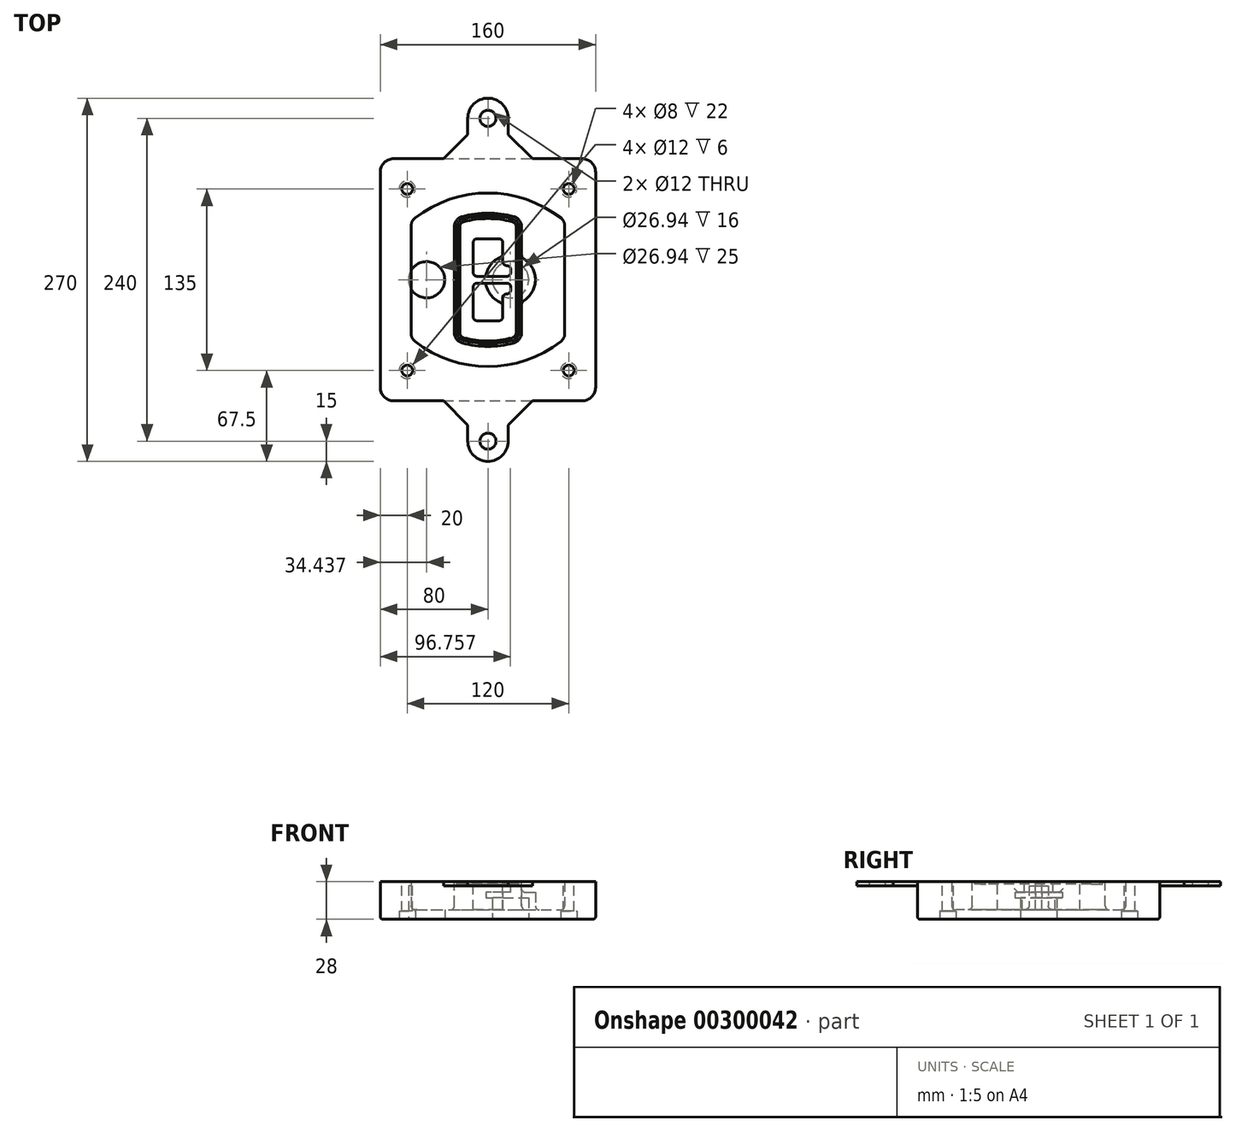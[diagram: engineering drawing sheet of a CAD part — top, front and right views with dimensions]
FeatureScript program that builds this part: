
annotation { "Feature Type Name" : "Feature", "Feature Type Description" : "" }
export const myFeature = defineFeature(function(context is Context, id is Id, definition is map)
    precondition{}
    {
        {
            var Q0;
            Q0=qCreatedBy(makeId("Top.planeOp"),FACE);
            var sketch = newSketch(context, id + "F0", { "sketchPlane" : qUnion([Q0])});
            skPoint(sketch, "E0.rect.middle", {"position": v(0, 0) * mm});
            skLineSegment(sketch, "E1.bottom", {"start": v(-70, -90) * mm, "end": v(70, -90) * mm});
            skLineSegment(sketch, "E1.top", {"start": v(-70, 90) * mm, "end": v(70, 90) * mm});
            skLineSegment(sketch, "E1.left", {"start": v(-80, -80) * mm, "end": v(-80, 80) * mm});
            skLineSegment(sketch, "E1.right", {"start": v(80, -80) * mm, "end": v(80, 80) * mm});
            skLineSegment(sketch, "E2", {"start": v(-80, 90) * mm, "end": v(80, -90) * mm, "construction": true});
            skLineSegment(sketch, "E3", {"start": v(80, 90) * mm, "end": v(-80, -90) * mm, "construction": true});
            skCircle(sketch, "E4", {"center": v(-60, 67.5) * mm, "radius": 4 * mm});
            skCircle(sketch, "E5", {"center": v(60, 67.5) * mm, "radius": 4 * mm});
            skCircle(sketch, "E6", {"center": v(60, -67.5) * mm, "radius": 4 * mm});
            skCircle(sketch, "E7", {"center": v(-60, -67.5) * mm, "radius": 4 * mm});
            skLineSegment(sketch, "E8", {"start": v(-60, 67.5) * mm, "end": v(60, 67.5) * mm, "construction": true});
            skLineSegment(sketch, "E9", {"start": v(60, 67.5) * mm, "end": v(60, -67.5) * mm, "construction": true});
            skLineSegment(sketch, "E10", {"start": v(60, -67.5) * mm, "end": v(-60, -67.5) * mm, "construction": true});
            skLineSegment(sketch, "E11", {"start": v(-60, -67.5) * mm, "end": v(-60, 67.5) * mm, "construction": true});
            skLineSegment(sketch, "E12", {"start": v(-60, 40.3) * mm, "end": v(-60, -40.3) * mm});
            skLineSegment(sketch, "E13", {"start": v(60, 40.3) * mm, "end": v(60, -40.3) * mm});
            skArc(sketch, "E14", {"start": v(56.15, 48.18) * mm, "mid": v(0, 67.5) * mm, "end": v(-56.15, 48.18) * mm});
            skArc(sketch, "E15", {"start": v(-56.15, -48.18) * mm, "mid": v(0, -67.5) * mm, "end": v(56.15, -48.18) * mm});
            skLineSegment(sketch, "E16", {"start": v(-60, 0) * mm, "end": v(60, 0) * mm, "construction": true});
            skPoint(sketch, "E17.visualSharp", {"position": v(-60, -45) * mm});
            skArc(sketch, "E17.filletArc", {"start": v(-60, -40.3) * mm, "mid": v(-58.99, -44.68) * mm, "end": v(-56.15, -48.18) * mm});
            skPoint(sketch, "E18.visualSharp", {"position": v(-60, 45) * mm});
            skArc(sketch, "E18.filletArc", {"start": v(-56.15, 48.18) * mm, "mid": v(-58.99, 44.68) * mm, "end": v(-60, 40.3) * mm});
            skPoint(sketch, "E19.visualSharp", {"position": v(60, 45) * mm});
            skArc(sketch, "E19.filletArc", {"start": v(60, 40.3) * mm, "mid": v(58.99, 44.68) * mm, "end": v(56.15, 48.18) * mm});
            skPoint(sketch, "E20.visualSharp", {"position": v(60, -45) * mm});
            skArc(sketch, "E20.filletArc", {"start": v(56.15, -48.18) * mm, "mid": v(58.99, -44.68) * mm, "end": v(60, -40.3) * mm});
            skPoint(sketch, "E21.visualSharp", {"position": v(-80, 90) * mm});
            skArc(sketch, "E21.filletArc", {"start": v(-70, 90) * mm, "mid": v(-77.07, 87.07) * mm, "end": v(-80, 80) * mm});
            skPoint(sketch, "E22.visualSharp", {"position": v(80, 90) * mm});
            skArc(sketch, "E22.filletArc", {"start": v(80, 80) * mm, "mid": v(77.07, 87.07) * mm, "end": v(70, 90) * mm});
            skPoint(sketch, "E23.visualSharp", {"position": v(80, -90) * mm});
            skArc(sketch, "E23.filletArc", {"start": v(70, -90) * mm, "mid": v(77.07, -87.07) * mm, "end": v(80, -80) * mm});
            skPoint(sketch, "E24.visualSharp", {"position": v(-80, -90) * mm});
            skArc(sketch, "E24.filletArc", {"start": v(-80, -80) * mm, "mid": v(-77.07, -87.07) * mm, "end": v(-70, -90) * mm});
            skArc(sketch, "E25.0", {"start": v(57, 40.3) * mm, "mid": v(56.3, 43.36) * mm, "end": v(54.3, 45.81) * mm});
            skLineSegment(sketch, "E25.1", {"start": v(57, 40.3) * mm, "end": v(57, -40.3) * mm});
            skArc(sketch, "E25.2", {"start": v(54.3, -45.81) * mm, "mid": v(56.3, -43.36) * mm, "end": v(57, -40.3) * mm});
            skArc(sketch, "E25.3", {"start": v(-54.3, -45.81) * mm, "mid": v(0, -64.5) * mm, "end": v(54.3, -45.81) * mm});
            skArc(sketch, "E25.4", {"start": v(-57, -40.3) * mm, "mid": v(-56.3, -43.36) * mm, "end": v(-54.3, -45.81) * mm});
            skArc(sketch, "E25.5", {"start": v(54.3, 45.81) * mm, "mid": v(0, 64.5) * mm, "end": v(-54.3, 45.81) * mm});
            skLineSegment(sketch, "E25.6", {"start": v(-57, 40.3) * mm, "end": v(-57, -40.3) * mm});
            skArc(sketch, "E25.7", {"start": v(-54.3, 45.81) * mm, "mid": v(-56.3, 43.36) * mm, "end": v(-57, 40.3) * mm});
            skArc(sketch, "E26.0", {"start": v(-58.62, 51.33) * mm, "mid": v(-62.58, 46.43) * mm, "end": v(-64, 40.3) * mm});
            skArc(sketch, "E26.1", {"start": v(58.62, 51.33) * mm, "mid": v(0, 71.5) * mm, "end": v(-58.62, 51.33) * mm});
            skArc(sketch, "E26.2", {"start": v(64, 40.3) * mm, "mid": v(62.58, 46.43) * mm, "end": v(58.62, 51.33) * mm});
            skLineSegment(sketch, "E26.3", {"start": v(64, 40.3) * mm, "end": v(64, -40.3) * mm});
            skArc(sketch, "E26.4", {"start": v(58.62, -51.33) * mm, "mid": v(62.58, -46.43) * mm, "end": v(64, -40.3) * mm});
            skLineSegment(sketch, "E26.5", {"start": v(-64, 40.3) * mm, "end": v(-64, -40.3) * mm});
            skArc(sketch, "E26.6", {"start": v(-58.62, -51.33) * mm, "mid": v(0, -71.5) * mm, "end": v(58.62, -51.33) * mm});
            skArc(sketch, "E26.7", {"start": v(-64, -40.3) * mm, "mid": v(-62.58, -46.43) * mm, "end": v(-58.62, -51.33) * mm});
            skSolve(sketch);
        }
        {
            var Q0;
            Q0=makeQuery(id+"F0.imprint","IMPRINT",FACE,{"disambiguationData":[TD([[makeQuery(id+"F0.imprint","IMPRINT",EDGE,{"derivedFrom":sQuery(id+"F0.wireOp",EDGE,"E1.bottom")}),1.0]])]});
            var Q1;
            Q1=makeQuery(id+"F0.imprint","IMPRINT",FACE,{"disambiguationData":[TD([[makeQuery(id+"F0.imprint","IMPRINT",EDGE,{"derivedFrom":sQuery(id+"F0.wireOp",EDGE,"E12")}),1.0]])]});
            var Q2;
            Q2=makeQuery(id+"F0.imprint","IMPRINT",FACE,{"disambiguationData":[TD([[makeQuery(id+"F0.imprint","IMPRINT",EDGE,{"derivedFrom":sQuery(id+"F0.wireOp",EDGE,"E25.0")}),1.0]])]});
            var Q3;
            Q3=makeQuery(id+"F0.imprint","IMPRINT",FACE,{"disambiguationData":[TD([[makeQuery(id+"F0.imprint","IMPRINT",EDGE,{"derivedFrom":sQuery(id+"F0.wireOp",EDGE,"E12")}),-1.0]])]});
            extrude(context, id + "F1", {"entities" : qUnion([Q0, Q1, Q2, Q3]), "oppositeDirection" : true, "depth" : 25 * mm});
        }
        {
            var Q0;
            Q0=makeQuery(id+"F0.imprint","IMPRINT",FACE,{"disambiguationData":[TD([[makeQuery(id+"F0.imprint","IMPRINT",EDGE,{"derivedFrom":sQuery(id+"F0.wireOp",EDGE,"E12")}),1.0]])]});
            extrude(context, id + "F2", {"entities" : qUnion([Q0]), "operationType" : NewBodyOperationType.ADD, "depth" : 3 * mm});
        }
        {
            var Q0;
            Q0=makeQuery(id+"F0.imprint","IMPRINT",FACE,{"disambiguationData":[TD([[makeQuery(id+"F0.imprint","IMPRINT",EDGE,{"derivedFrom":sQuery(id+"F0.wireOp",EDGE,"E25.0")}),1.0]])]});
            extrude(context, id + "F3", {"entities" : qUnion([Q0]), "operationType" : NewBodyOperationType.REMOVE, "oppositeDirection" : true, "depth" : 18 * mm});
        }
        {
            var Q0;
            Q0=makeQuery(id+"F2.opExtrude","CAP_FACE",FACE,{"disambiguationData":[OSD([sQuery(id+"F0.wireOp",EDGE,"E12"),sQuery(id+"F0.wireOp",EDGE,"E13"),sQuery(id+"F0.wireOp",EDGE,"E14"),sQuery(id+"F0.wireOp",EDGE,"E15"),sQuery(id+"F0.wireOp",EDGE,"E17.filletArc"),sQuery(id+"F0.wireOp",EDGE,"E18.filletArc"),sQuery(id+"F0.wireOp",EDGE,"E19.filletArc"),sQuery(id+"F0.wireOp",EDGE,"E20.filletArc"),sQuery(id+"F0.wireOp",EDGE,"E25.0"),sQuery(id+"F0.wireOp",EDGE,"E25.1"),sQuery(id+"F0.wireOp",EDGE,"E25.2"),sQuery(id+"F0.wireOp",EDGE,"E25.3"),sQuery(id+"F0.wireOp",EDGE,"E25.4"),sQuery(id+"F0.wireOp",EDGE,"E25.5"),sQuery(id+"F0.wireOp",EDGE,"E25.6"),sQuery(id+"F0.wireOp",EDGE,"E25.7")])],"isStart":false});
            var sketch = newSketch(context, id + "F4", { "sketchPlane" : qUnion([Q0])});
            skArc(sketch, "E27.0", {"start": v(-19.08, -46.97) * mm, "mid": v(0, -49.5) * mm, "end": v(19.08, -46.97) * mm});
            skArc(sketch, "E28.0", {"start": v(19.08, 46.97) * mm, "mid": v(0, 49.5) * mm, "end": v(-19.08, 46.97) * mm});
            skLineSegment(sketch, "E29", {"start": v(-25, 39.25) * mm, "end": v(-25, -39.25) * mm});
            skLineSegment(sketch, "E30", {"start": v(25, 39.25) * mm, "end": v(25, -39.25) * mm});
            skLineSegment(sketch, "E31", {"start": v(-25, 45.1) * mm, "end": v(25, 45.1) * mm, "construction": true});
            skLineSegment(sketch, "E32", {"start": v(-25, -45.1) * mm, "end": v(25, -45.1) * mm, "construction": true});
            skPoint(sketch, "E33.visualSharp", {"position": v(-25, 45.1) * mm});
            skArc(sketch, "E33.filletArc", {"start": v(-19.08, 46.97) * mm, "mid": v(-23.35, 44.11) * mm, "end": v(-25, 39.25) * mm});
            skPoint(sketch, "E34.visualSharp", {"position": v(25, 45.1) * mm});
            skArc(sketch, "E34.filletArc", {"start": v(25, 39.25) * mm, "mid": v(23.35, 44.11) * mm, "end": v(19.08, 46.97) * mm});
            skPoint(sketch, "E35.visualSharp", {"position": v(25, -45.1) * mm});
            skArc(sketch, "E35.filletArc", {"start": v(19.08, -46.97) * mm, "mid": v(23.35, -44.11) * mm, "end": v(25, -39.25) * mm});
            skPoint(sketch, "E36.visualSharp", {"position": v(-25, -45.1) * mm});
            skArc(sketch, "E36.filletArc", {"start": v(-25, -39.25) * mm, "mid": v(-23.35, -44.11) * mm, "end": v(-19.08, -46.97) * mm});
            skArc(sketch, "E37.0", {"start": v(54.3, 45.81) * mm, "mid": v(0, 64.5) * mm, "end": v(-54.3, 45.81) * mm});
            skArc(sketch, "E37.1", {"start": v(-54.3, 45.81) * mm, "mid": v(-56.3, 43.36) * mm, "end": v(-57, 40.3) * mm});
            skLineSegment(sketch, "E37.2", {"start": v(-57, 40.3) * mm, "end": v(-57, -40.3) * mm});
            skArc(sketch, "E37.3", {"start": v(-57, -40.3) * mm, "mid": v(-56.3, -43.36) * mm, "end": v(-54.3, -45.81) * mm});
            skArc(sketch, "E37.4", {"start": v(-54.3, -45.81) * mm, "mid": v(0, -64.5) * mm, "end": v(54.3, -45.81) * mm});
            skArc(sketch, "E37.5", {"start": v(54.3, -45.81) * mm, "mid": v(56.3, -43.36) * mm, "end": v(57, -40.3) * mm});
            skLineSegment(sketch, "E37.6", {"start": v(57, 40.3) * mm, "end": v(57, -40.3) * mm});
            skArc(sketch, "E37.7", {"start": v(57, 40.3) * mm, "mid": v(56.3, 43.36) * mm, "end": v(54.3, 45.81) * mm});
            skLineSegment(sketch, "E38.0", {"start": v(23, 39.25) * mm, "end": v(23, -39.25) * mm});
            skArc(sketch, "E38.1", {"start": v(18.56, -45.04) * mm, "mid": v(21.76, -42.9) * mm, "end": v(23, -39.25) * mm});
            skArc(sketch, "E38.2", {"start": v(-18.56, -45.04) * mm, "mid": v(0, -47.5) * mm, "end": v(18.56, -45.04) * mm});
            skArc(sketch, "E38.3", {"start": v(-23, -39.25) * mm, "mid": v(-21.76, -42.9) * mm, "end": v(-18.56, -45.04) * mm});
            skLineSegment(sketch, "E38.4", {"start": v(-23, 39.25) * mm, "end": v(-23, -39.25) * mm});
            skArc(sketch, "E38.5", {"start": v(23, 39.25) * mm, "mid": v(21.76, 42.9) * mm, "end": v(18.56, 45.04) * mm});
            skArc(sketch, "E38.6", {"start": v(-18.56, 45.04) * mm, "mid": v(-21.76, 42.9) * mm, "end": v(-23, 39.25) * mm});
            skArc(sketch, "E38.7", {"start": v(18.56, 45.04) * mm, "mid": v(0, 47.5) * mm, "end": v(-18.56, 45.04) * mm});
            skArc(sketch, "E39.0", {"start": v(21, 39.25) * mm, "mid": v(20.18, 41.68) * mm, "end": v(18.04, 43.1) * mm});
            skLineSegment(sketch, "E39.1", {"start": v(21, 39.25) * mm, "end": v(21, -39.25) * mm});
            skArc(sketch, "E39.2", {"start": v(18.04, -43.1) * mm, "mid": v(20.18, -41.68) * mm, "end": v(21, -39.25) * mm});
            skArc(sketch, "E39.3", {"start": v(-18.04, -43.1) * mm, "mid": v(0, -45.5) * mm, "end": v(18.04, -43.1) * mm});
            skArc(sketch, "E39.4", {"start": v(-21, -39.25) * mm, "mid": v(-20.18, -41.68) * mm, "end": v(-18.04, -43.1) * mm});
            skArc(sketch, "E39.5", {"start": v(18.04, 43.1) * mm, "mid": v(0, 45.5) * mm, "end": v(-18.04, 43.1) * mm});
            skLineSegment(sketch, "E39.6", {"start": v(-21, 39.25) * mm, "end": v(-21, -39.25) * mm});
            skArc(sketch, "E39.7", {"start": v(-18.04, 43.1) * mm, "mid": v(-20.18, 41.68) * mm, "end": v(-21, 39.25) * mm});
            skLineSegment(sketch, "E40", {"start": v(-25, 0) * mm, "end": v(25, 0) * mm, "construction": true});
            skLineSegment(sketch, "E41", {"start": v(-11, 5.5) * mm, "end": v(-11, 27.5) * mm});
            skLineSegment(sketch, "E42", {"start": v(-8, 30.5) * mm, "end": v(8, 30.5) * mm});
            skLineSegment(sketch, "E43", {"start": v(11, 27.5) * mm, "end": v(11, 13.5) * mm});
            skLineSegment(sketch, "E44", {"start": v(14, 10.5) * mm, "end": v(14, 10.5) * mm});
            skLineSegment(sketch, "E45", {"start": v(17, 7.5) * mm, "end": v(17, 5.5) * mm});
            skLineSegment(sketch, "E46", {"start": v(14, 2.5) * mm, "end": v(-8, 2.5) * mm});
            skPoint(sketch, "E47.visualSharp", {"position": v(-11, 30.5) * mm});
            skArc(sketch, "E47.filletArc", {"start": v(-8, 30.5) * mm, "mid": v(-10.12, 29.62) * mm, "end": v(-11, 27.5) * mm});
            skPoint(sketch, "E48.visualSharp", {"position": v(11, 30.5) * mm});
            skArc(sketch, "E48.filletArc", {"start": v(11, 27.5) * mm, "mid": v(10.12, 29.62) * mm, "end": v(8, 30.5) * mm});
            skPoint(sketch, "E49.visualSharp", {"position": v(11, 10.5) * mm});
            skArc(sketch, "E49.filletArc", {"start": v(11, 13.5) * mm, "mid": v(11.88, 11.38) * mm, "end": v(14, 10.5) * mm});
            skPoint(sketch, "E50.visualSharp", {"position": v(17, 10.5) * mm});
            skArc(sketch, "E50.filletArc", {"start": v(17, 7.5) * mm, "mid": v(16.12, 9.62) * mm, "end": v(14, 10.5) * mm});
            skPoint(sketch, "E51.visualSharp", {"position": v(17, 2.5) * mm});
            skArc(sketch, "E51.filletArc", {"start": v(14, 2.5) * mm, "mid": v(16.12, 3.38) * mm, "end": v(17, 5.5) * mm});
            skPoint(sketch, "E52.visualSharp", {"position": v(-11, 2.5) * mm});
            skArc(sketch, "E52.filletArc", {"start": v(-11, 5.5) * mm, "mid": v(-10.12, 3.38) * mm, "end": v(-8, 2.5) * mm});
            skLineSegment(sketch, "E53.0.MirrorCS", {"start": v(14, -2.5) * mm, "end": v(-8, -2.5) * mm});
            skArc(sketch, "E54.0.MirrorCS", {"start": v(-11, -5.5) * mm, "mid": v(-10.12, -3.38) * mm, "end": v(-8, -2.5) * mm});
            skLineSegment(sketch, "E55.0.MirrorCS", {"start": v(-11, -5.5) * mm, "end": v(-11, -27.5) * mm});
            skArc(sketch, "E56.0.MirrorCS", {"start": v(-8, -30.5) * mm, "mid": v(-10.12, -29.62) * mm, "end": v(-11, -27.5) * mm});
            skLineSegment(sketch, "E57.0.MirrorCS", {"start": v(-8, -30.5) * mm, "end": v(8, -30.5) * mm});
            skArc(sketch, "E58.0.MirrorCS", {"start": v(11, -27.5) * mm, "mid": v(10.12, -29.62) * mm, "end": v(8, -30.5) * mm});
            skLineSegment(sketch, "E59.0.MirrorCS", {"start": v(11, -27.5) * mm, "end": v(11, -13.5) * mm});
            skArc(sketch, "E60.0.MirrorCS", {"start": v(11, -13.5) * mm, "mid": v(11.88, -11.38) * mm, "end": v(14, -10.5) * mm});
            skArc(sketch, "E61.0.MirrorCS", {"start": v(17, -7.5) * mm, "mid": v(16.12, -9.62) * mm, "end": v(14, -10.5) * mm});
            skLineSegment(sketch, "E62.0.MirrorCS", {"start": v(17, -7.5) * mm, "end": v(17, -5.5) * mm});
            skArc(sketch, "E63.0.MirrorCS", {"start": v(14, -2.5) * mm, "mid": v(16.12, -3.38) * mm, "end": v(17, -5.5) * mm});
            skSolve(sketch);
        }
        {
            var Q0;
            Q0=makeQuery(id+"F4.imprint","IMPRINT",FACE,{"disambiguationData":[TD([[makeQuery(id+"F4.imprint","IMPRINT",EDGE,{"derivedFrom":sQuery(id+"F4.wireOp",EDGE,"E27.0")}),1.0]])]});
            var Q1;
            Q1=makeQuery(id+"F4.imprint","IMPRINT",FACE,{"disambiguationData":[TD([[makeQuery(id+"F4.imprint","IMPRINT",EDGE,{"derivedFrom":sQuery(id+"F4.wireOp",EDGE,"E38.0")}),-1.0]])]});
            var Q2;
            Q2=makeQuery(id+"F4.imprint","IMPRINT",FACE,{"disambiguationData":[TD([[makeQuery(id+"F4.imprint","IMPRINT",EDGE,{"derivedFrom":sQuery(id+"F4.wireOp",EDGE,"E39.0")}),1.0]])]});
            extrude(context, id + "F5", {"entities" : qUnion([Q0, Q1, Q2]), "operationType" : NewBodyOperationType.ADD, "endBound" : BoundingType.UP_TO_NEXT, "oppositeDirection" : true, "depth" : 25 * mm});
        }
        {
            var Q0;
            Q0=makeQuery(id+"F4.imprint","IMPRINT",FACE,{"disambiguationData":[TD([[makeQuery(id+"F4.imprint","IMPRINT",EDGE,{"derivedFrom":sQuery(id+"F4.wireOp",EDGE,"E38.0")}),-1.0]])]});
            extrude(context, id + "F6", {"entities" : qUnion([Q0]), "operationType" : NewBodyOperationType.REMOVE, "oppositeDirection" : true, "depth" : 2 * mm});
        }
        {
            var Q0;
            Q0=makeQuery(id+"F1.opExtrude","CAP_FACE",FACE,{"disambiguationData":[OSD([sQuery(id+"F0.wireOp",EDGE,"E1.bottom"),sQuery(id+"F0.wireOp",EDGE,"E1.top"),sQuery(id+"F0.wireOp",EDGE,"E1.left"),sQuery(id+"F0.wireOp",EDGE,"E1.right"),sQuery(id+"F0.wireOp",EDGE,"E4"),sQuery(id+"F0.wireOp",EDGE,"E5"),sQuery(id+"F0.wireOp",EDGE,"E6"),sQuery(id+"F0.wireOp",EDGE,"E7"),sQuery(id+"F0.wireOp",EDGE,"E21.filletArc"),sQuery(id+"F0.wireOp",EDGE,"E22.filletArc"),sQuery(id+"F0.wireOp",EDGE,"E23.filletArc"),sQuery(id+"F0.wireOp",EDGE,"E24.filletArc")])],"isStart":false});
            var sketch = newSketch(context, id + "F7", { "sketchPlane" : qUnion([Q0])});
            skCircle(sketch, "E64", {"center": v(16.76, 0) * mm, "radius": 13.47 * mm});
            skCircle(sketch, "E65", {"center": v(-45.56, 0) * mm, "radius": 13.47 * mm});
            skLineSegment(sketch, "E66", {"start": v(80, 0) * mm, "end": v(-80, 0) * mm});
            skCircle(sketch, "E67", {"center": v(16.76, 0) * mm, "radius": 18.47 * mm});
            skCircle(sketch, "E68", {"center": v(60, -67.5) * mm, "radius": 6 * mm});
            skCircle(sketch, "E69", {"center": v(-60, -67.5) * mm, "radius": 6 * mm});
            skCircle(sketch, "E70", {"center": v(-60, 67.5) * mm, "radius": 6 * mm});
            skCircle(sketch, "E71", {"center": v(60, 67.5) * mm, "radius": 6 * mm});
            skSolve(sketch);
        }
        {
            var Q0;
            {var subQ1=sQuery(id+"F7.wireOp",EDGE,"E66");var subQ4=sQuery(id+"F7.wireOp",EDGE,"E64");var subQ6=makeQuery(id+"F7.imprint","INTERSECT",VERTEX,{"disambiguationData":[OD(0.0)],"derivedFrom":[subQ4,subQ1]});Q0=makeQuery(id+"F7.imprint","IMPRINT",FACE,{"disambiguationData":[TD([[makeQuery(id+"F7.imprint","IMPRINT",EDGE,{"disambiguationData":[TD([[subQ6,-1.0]])],"derivedFrom":subQ4}),-1.0]])]});}
            var Q1;
            {var subQ0=sQuery(id+"F7.wireOp",EDGE,"E66");var subQ1=sQuery(id+"F7.wireOp",EDGE,"E64");var subQ3=makeQuery(id+"F7.imprint","INTERSECT",VERTEX,{"disambiguationData":[OD(0.0)],"derivedFrom":[subQ1,subQ0]});Q1=makeQuery(id+"F7.imprint","IMPRINT",FACE,{"disambiguationData":[TD([[makeQuery(id+"F7.imprint","IMPRINT",EDGE,{"disambiguationData":[TD([[subQ3,-1.0]])],"derivedFrom":subQ1}),1.0]])]});}
            var Q2;
            {var subQ0=sQuery(id+"F7.wireOp",EDGE,"E66");var subQ1=sQuery(id+"F7.wireOp",EDGE,"E64");var subQ3=makeQuery(id+"F7.imprint","INTERSECT",VERTEX,{"disambiguationData":[OD(0.0)],"derivedFrom":[subQ1,subQ0]});Q2=makeQuery(id+"F7.imprint","IMPRINT",FACE,{"disambiguationData":[TD([[makeQuery(id+"F7.imprint","IMPRINT",EDGE,{"disambiguationData":[TD([[subQ3,1.0]])],"derivedFrom":subQ1}),1.0]])]});}
            var Q3;
            {var subQ1=sQuery(id+"F7.wireOp",EDGE,"E66");var subQ4=sQuery(id+"F7.wireOp",EDGE,"E64");var subQ6=makeQuery(id+"F7.imprint","INTERSECT",VERTEX,{"disambiguationData":[OD(0.0)],"derivedFrom":[subQ4,subQ1]});Q3=makeQuery(id+"F7.imprint","IMPRINT",FACE,{"disambiguationData":[TD([[makeQuery(id+"F7.imprint","IMPRINT",EDGE,{"disambiguationData":[TD([[subQ6,1.0]])],"derivedFrom":subQ4}),-1.0]])]});}
            extrude(context, id + "F8", {"entities" : qUnion([Q0, Q1, Q2, Q3]), "operationType" : NewBodyOperationType.ADD, "oppositeDirection" : true, "depth" : 20 * mm});
        }
        {
            var Q0;
            {var subQ0=sQuery(id+"F7.wireOp",EDGE,"E66");var subQ1=sQuery(id+"F7.wireOp",EDGE,"E64");var subQ3=makeQuery(id+"F7.imprint","INTERSECT",VERTEX,{"disambiguationData":[OD(0.0)],"derivedFrom":[subQ1,subQ0]});Q0=makeQuery(id+"F7.imprint","IMPRINT",FACE,{"disambiguationData":[TD([[makeQuery(id+"F7.imprint","IMPRINT",EDGE,{"disambiguationData":[TD([[subQ3,-1.0]])],"derivedFrom":subQ1}),1.0]])]});}
            var Q1;
            {var subQ0=sQuery(id+"F7.wireOp",EDGE,"E66");var subQ1=sQuery(id+"F7.wireOp",EDGE,"E64");var subQ3=makeQuery(id+"F7.imprint","INTERSECT",VERTEX,{"disambiguationData":[OD(0.0)],"derivedFrom":[subQ1,subQ0]});Q1=makeQuery(id+"F7.imprint","IMPRINT",FACE,{"disambiguationData":[TD([[makeQuery(id+"F7.imprint","IMPRINT",EDGE,{"disambiguationData":[TD([[subQ3,1.0]])],"derivedFrom":subQ1}),1.0]])]});}
            extrude(context, id + "F9", {"entities" : qUnion([Q0, Q1]), "operationType" : NewBodyOperationType.REMOVE, "oppositeDirection" : true, "depth" : 16 * mm});
        }
        {
            var Q0;
            {var subQ0=sQuery(id+"F7.wireOp",EDGE,"E66");var subQ1=sQuery(id+"F7.wireOp",EDGE,"E65");var subQ3=makeQuery(id+"F7.imprint","INTERSECT",VERTEX,{"disambiguationData":[OD(0.0)],"derivedFrom":[subQ1,subQ0]});Q0=makeQuery(id+"F7.imprint","IMPRINT",FACE,{"disambiguationData":[TD([[makeQuery(id+"F7.imprint","IMPRINT",EDGE,{"disambiguationData":[TD([[subQ3,-1.0]])],"derivedFrom":subQ1}),1.0]])]});}
            var Q1;
            {var subQ0=sQuery(id+"F7.wireOp",EDGE,"E66");var subQ1=sQuery(id+"F7.wireOp",EDGE,"E65");var subQ3=makeQuery(id+"F7.imprint","INTERSECT",VERTEX,{"disambiguationData":[OD(0.0)],"derivedFrom":[subQ1,subQ0]});Q1=makeQuery(id+"F7.imprint","IMPRINT",FACE,{"disambiguationData":[TD([[makeQuery(id+"F7.imprint","IMPRINT",EDGE,{"disambiguationData":[TD([[subQ3,1.0]])],"derivedFrom":subQ1}),1.0]])]});}
            extrude(context, id + "F10", {"entities" : qUnion([Q0, Q1]), "operationType" : NewBodyOperationType.REMOVE, "oppositeDirection" : true, "depth" : 25 * mm});
        }
        {
            var Q0;
            Q0=makeQuery(id+"F7.imprint","IMPRINT",FACE,{"disambiguationData":[TD([[makeQuery(id+"F7.imprint","IMPRINT",EDGE,{"derivedFrom":sQuery(id+"F7.wireOp",EDGE,"E68")}),1.0]])]});
            var Q1;
            Q1=makeQuery(id+"F7.imprint","IMPRINT",FACE,{"disambiguationData":[TD([[makeQuery(id+"F7.imprint","IMPRINT",EDGE,{"derivedFrom":makeQuery(id+"F1.opExtrude","CAP_EDGE",EDGE,{"disambiguationData":[OSD([sQuery(id+"F0.wireOp",EDGE,"E5")])],"isStart":false})}),-1.0]])]});
            var Q2;
            Q2=makeQuery(id+"F7.imprint","IMPRINT",FACE,{"disambiguationData":[TD([[makeQuery(id+"F7.imprint","IMPRINT",EDGE,{"derivedFrom":sQuery(id+"F7.wireOp",EDGE,"E69")}),1.0]])]});
            var Q3;
            Q3=makeQuery(id+"F7.imprint","IMPRINT",FACE,{"disambiguationData":[TD([[makeQuery(id+"F7.imprint","IMPRINT",EDGE,{"derivedFrom":makeQuery(id+"F1.opExtrude","CAP_EDGE",EDGE,{"disambiguationData":[OSD([sQuery(id+"F0.wireOp",EDGE,"E4")])],"isStart":false})}),-1.0]])]});
            var Q4;
            Q4=makeQuery(id+"F7.imprint","IMPRINT",FACE,{"disambiguationData":[TD([[makeQuery(id+"F7.imprint","IMPRINT",EDGE,{"derivedFrom":sQuery(id+"F7.wireOp",EDGE,"E70")}),1.0]])]});
            var Q5;
            Q5=makeQuery(id+"F7.imprint","IMPRINT",FACE,{"disambiguationData":[TD([[makeQuery(id+"F7.imprint","IMPRINT",EDGE,{"derivedFrom":makeQuery(id+"F1.opExtrude","CAP_EDGE",EDGE,{"disambiguationData":[OSD([sQuery(id+"F0.wireOp",EDGE,"E7")])],"isStart":false})}),-1.0]])]});
            var Q6;
            Q6=makeQuery(id+"F7.imprint","IMPRINT",FACE,{"disambiguationData":[TD([[makeQuery(id+"F7.imprint","IMPRINT",EDGE,{"derivedFrom":sQuery(id+"F7.wireOp",EDGE,"E71")}),1.0]])]});
            var Q7;
            Q7=makeQuery(id+"F7.imprint","IMPRINT",FACE,{"disambiguationData":[TD([[makeQuery(id+"F7.imprint","IMPRINT",EDGE,{"derivedFrom":makeQuery(id+"F1.opExtrude","CAP_EDGE",EDGE,{"disambiguationData":[OSD([sQuery(id+"F0.wireOp",EDGE,"E6")])],"isStart":false})}),-1.0]])]});
            extrude(context, id + "F11", {"entities" : qUnion([Q0, Q1, Q2, Q3, Q4, Q5, Q6, Q7]), "operationType" : NewBodyOperationType.REMOVE, "oppositeDirection" : true, "depth" : 6 * mm});
        }
        {
            var Q0;
            Q0=makeQuery(id+"F9.boolean.opBoolean","COPY",FACE,{"derivedFrom":makeQuery(id+"F9.opExtrude","CAP_FACE",FACE,{"disambiguationData":[OSD([sQuery(id+"F7.wireOp",EDGE,"E64")])],"isStart":false})});
            var sketch = newSketch(context, id + "F12", { "sketchPlane" : qUnion([Q0])});
            skArc(sketch, "E72.0", {"start": v(11, 17.55) * mm, "mid": v(2.57, 11.82) * mm, "end": v(-1.54, 2.5) * mm});
            skArc(sketch, "E72.1", {"start": v(-1.54, -2.5) * mm, "mid": v(2.57, -11.82) * mm, "end": v(11, -17.55) * mm});
            skLineSegment(sketch, "E73", {"start": v(-1.54, -2.5) * mm, "end": v(14, -2.5) * mm});
            skLineSegment(sketch, "E74.0", {"start": v(14, 2.5) * mm, "end": v(-1.54, 2.5) * mm});
            skArc(sketch, "E74.1", {"start": v(14, 2.5) * mm, "mid": v(16.12, 3.38) * mm, "end": v(17, 5.5) * mm});
            skLineSegment(sketch, "E74.2", {"start": v(17, 7.5) * mm, "end": v(17, 5.5) * mm});
            skArc(sketch, "E74.3", {"start": v(17, 7.5) * mm, "mid": v(16.12, 9.62) * mm, "end": v(14, 10.5) * mm});
            skArc(sketch, "E74.4", {"start": v(11, 13.5) * mm, "mid": v(11.88, 11.38) * mm, "end": v(14, 10.5) * mm});
            skLineSegment(sketch, "E74.5", {"start": v(11, 17.55) * mm, "end": v(11, 13.5) * mm});
            skLineSegment(sketch, "E74.7", {"start": v(14, -2.5) * mm, "end": v(-1.54, -2.5) * mm});
            skArc(sketch, "E74.8", {"start": v(14, -2.5) * mm, "mid": v(16.12, -3.38) * mm, "end": v(17, -5.5) * mm});
            skLineSegment(sketch, "E74.9", {"start": v(17, -7.5) * mm, "end": v(17, -5.5) * mm});
            skArc(sketch, "E74.10", {"start": v(17, -7.5) * mm, "mid": v(16.12, -9.62) * mm, "end": v(14, -10.5) * mm});
            skArc(sketch, "E74.11", {"start": v(11, -13.5) * mm, "mid": v(11.88, -11.38) * mm, "end": v(14, -10.5) * mm});
            skLineSegment(sketch, "E74.12", {"start": v(11, -17.55) * mm, "end": v(11, -13.5) * mm});
            skPoint(sketch, "E75.orphan", {"position": v(11, -27.5) * mm});
            skPoint(sketch, "E76.orphan", {"position": v(-8, -2.5) * mm});
            skPoint(sketch, "E77.orphan", {"position": v(-8, 2.5) * mm});
            skPoint(sketch, "E78.orphan", {"position": v(11, 27.5) * mm});
            skSolve(sketch);
        }
        {
            var Q0;
            {var subQ7=sQuery(id+"F12.wireOp",EDGE,"E72.0");var subQ14=sQuery(id+"F12.wireOp",EDGE,"E72.1");var subQ16=sQuery(id+"F12.wireOp",EDGE,"E74.1");var subQ18=sQuery(id+"F12.wireOp",EDGE,"E74.8");Q0=qUnion([makeQuery(id+"F12.imprint","IMPRINT",FACE,{"disambiguationData":[TD([[makeQuery(id+"F12.imprint","IMPRINT",EDGE,{"derivedFrom":subQ7}),1.0]])]}),makeQuery(id+"F12.imprint","IMPRINT",FACE,{"disambiguationData":[TD([[makeQuery(id+"F12.imprint","IMPRINT",EDGE,{"derivedFrom":subQ14}),1.0]])]}),makeQuery(id+"F12.imprint","IMPRINT",FACE,{"disambiguationData":[TD([[makeQuery(id+"F12.imprint","IMPRINT",EDGE,{"derivedFrom":subQ16}),1.0]])]}),makeQuery(id+"F12.imprint","IMPRINT",FACE,{"disambiguationData":[TD([[makeQuery(id+"F12.imprint","IMPRINT",EDGE,{"derivedFrom":subQ18}),-1.0]])]})]);}
            var Q1;
            Q1=makeQuery(id+"F5.boolean.opBoolean","SPLIT",FACE,{"disambiguationData":[TD([makeQuery(id+"F5.opExtrude","SWEPT_FACE",FACE,{"disambiguationData":[OSD([sQuery(id+"F4.wireOp",EDGE,"E41")])]})])],"derivedFrom":makeQuery(id+"F3.boolean.opBoolean","COPY",FACE,{"derivedFrom":makeQuery(id+"F3.opExtrude","CAP_FACE",FACE,{"disambiguationData":[OSD([sQuery(id+"F0.wireOp",EDGE,"E25.0"),sQuery(id+"F0.wireOp",EDGE,"E25.1"),sQuery(id+"F0.wireOp",EDGE,"E25.2"),sQuery(id+"F0.wireOp",EDGE,"E25.3"),sQuery(id+"F0.wireOp",EDGE,"E25.4"),sQuery(id+"F0.wireOp",EDGE,"E25.5"),sQuery(id+"F0.wireOp",EDGE,"E25.6"),sQuery(id+"F0.wireOp",EDGE,"E25.7")])],"isStart":false})})});
            extrude(context, id + "F13", {"entities" : qUnion([Q0]), "operationType" : NewBodyOperationType.REMOVE, "endBound" : BoundingType.UP_TO_SURFACE, "endBoundEntityFace" : qUnion([Q1]), "depth" : 25 * mm});
        }
        {
            var Q0;
            Q0=makeQuery(id+"F3.boolean.opBoolean","COPY",EDGE,{"derivedFrom":makeQuery(id+"F3.opExtrude","CAP_EDGE",EDGE,{"disambiguationData":[OSD([sQuery(id+"F0.wireOp",EDGE,"E25.6")])],"isStart":false})});
            var Q1;
            Q1=makeQuery(id+"F8.boolean.opBoolean","INTERSECT",EDGE,{"derivedFrom":[makeQuery(id+"F5.opExtrude","SWEPT_FACE",FACE,{"disambiguationData":[OSD([sQuery(id+"F4.wireOp",EDGE,"E30")])]}),makeQuery(id+"F8.opExtrude","CAP_FACE",FACE,{"disambiguationData":[OSD([sQuery(id+"F7.wireOp",EDGE,"E67")])],"isStart":false})]});
            var Q2;
            Q2=makeQuery(id+"F8.boolean.opBoolean","INTERSECT",EDGE,{"disambiguationData":[OD(1.0)],"derivedFrom":[makeQuery(id+"F5.opExtrude","SWEPT_FACE",FACE,{"disambiguationData":[OSD([sQuery(id+"F4.wireOp",EDGE,"E30")])]}),makeQuery(id+"F8.opExtrude","SWEPT_FACE",FACE,{"disambiguationData":[OSD([sQuery(id+"F7.wireOp",EDGE,"E67")])]})]});
            var Q3;
            {var subQ0=sQuery(id+"F4.wireOp",EDGE,"E30");Q3=makeQuery(id+"F8.boolean.opBoolean","SPLIT",EDGE,{"disambiguationData":[TD([makeQuery(id+"F5.opExtrude","SWEPT_FACE",FACE,{"disambiguationData":[OSD([sQuery(id+"F4.wireOp",EDGE,"E35.filletArc")])]})])],"derivedFrom":makeQuery(id+"F5.opExtrude","CAP_EDGE",EDGE,{"disambiguationData":[OSD([subQ0])],"isStart":false})});}
            var Q4;
            {var subQ0=sQuery(id+"F0.wireOp",EDGE,"E25.7");var subQ1=sQuery(id+"F0.wireOp",EDGE,"E25.1");var subQ2=sQuery(id+"F0.wireOp",EDGE,"E25.6");var subQ3=sQuery(id+"F0.wireOp",EDGE,"E25.5");var subQ4=sQuery(id+"F0.wireOp",EDGE,"E25.4");var subQ5=sQuery(id+"F0.wireOp",EDGE,"E25.0");var subQ6=sQuery(id+"F0.wireOp",EDGE,"E25.2");var subQ7=sQuery(id+"F0.wireOp",EDGE,"E25.3");Q4=makeQuery(id+"F8.boolean.opBoolean","INTERSECT",EDGE,{"derivedFrom":[makeQuery(id+"F5.boolean.opBoolean","SPLIT",FACE,{"disambiguationData":[TD([makeQuery(id+"F2.opExtrude","SWEPT_FACE",FACE,{"disambiguationData":[OSD([subQ5])]})])],"derivedFrom":makeQuery(id+"F3.boolean.opBoolean","COPY",FACE,{"derivedFrom":makeQuery(id+"F3.opExtrude","CAP_FACE",FACE,{"disambiguationData":[OSD([subQ5,subQ1,subQ6,subQ7,subQ4,subQ3,subQ2,subQ0])],"isStart":false})})}),makeQuery(id+"F8.opExtrude","SWEPT_FACE",FACE,{"disambiguationData":[OSD([sQuery(id+"F7.wireOp",EDGE,"E67")])]})]});}
            var Q5;
            Q5=makeQuery(id+"F8.boolean.opBoolean","INTERSECT",EDGE,{"disambiguationData":[OD(0.0)],"derivedFrom":[makeQuery(id+"F5.opExtrude","SWEPT_FACE",FACE,{"disambiguationData":[OSD([sQuery(id+"F4.wireOp",EDGE,"E30")])]}),makeQuery(id+"F8.opExtrude","SWEPT_FACE",FACE,{"disambiguationData":[OSD([sQuery(id+"F7.wireOp",EDGE,"E67")])]})]});
            fillet(context, id + "F14", {"entities" : qUnion([Q0, Q1, Q2, Q3, Q4, Q5]), "radius" : 3 * mm, "tangentPropagation" : true, "allowEdgeOverflow" : false});
        }
        {
            var Q0;
            Q0=makeQuery(id+"F1.opExtrude","CAP_EDGE",EDGE,{"disambiguationData":[OSD([sQuery(id+"F0.wireOp",EDGE,"E1.bottom")])],"isStart":false});
            fillet(context, id + "F15", {"entities" : qUnion([Q0]), "radius" : 2 * mm, "tangentPropagation" : true, "allowEdgeOverflow" : false});
        }
        {
            var Q0;
            {var subQ0=sQuery(id+"F0.wireOp",EDGE,"E21.filletArc");var subQ1=sQuery(id+"F0.wireOp",EDGE,"E7");var subQ2=sQuery(id+"F0.wireOp",EDGE,"E6");var subQ3=sQuery(id+"F0.wireOp",EDGE,"E5");var subQ4=sQuery(id+"F0.wireOp",EDGE,"E4");var subQ5=sQuery(id+"F0.wireOp",EDGE,"E22.filletArc");var subQ6=sQuery(id+"F0.wireOp",EDGE,"E1.bottom");var subQ7=sQuery(id+"F0.wireOp",EDGE,"E1.right");var subQ8=sQuery(id+"F0.wireOp",EDGE,"E1.top");var subQ9=sQuery(id+"F0.wireOp",EDGE,"E1.left");var subQ10=sQuery(id+"F0.wireOp",EDGE,"E23.filletArc");var subQ11=sQuery(id+"F0.wireOp",EDGE,"E24.filletArc");Q0=makeQuery(id+"F2.boolean.opBoolean","SPLIT",FACE,{"disambiguationData":[TD([makeQuery(id+"F1.opExtrude","SWEPT_FACE",FACE,{"disambiguationData":[OSD([subQ6])]})])],"derivedFrom":makeQuery(id+"F1.opExtrude","CAP_FACE",FACE,{"disambiguationData":[OSD([subQ6,subQ8,subQ9,subQ7,subQ4,subQ3,subQ2,subQ1,subQ0,subQ5,subQ10,subQ11])],"isStart":true})});}
            var sketch = newSketch(context, id + "F16", { "sketchPlane" : qUnion([Q0])});
            skLineSegment(sketch, "E79", {"start": v(-33, 90) * mm, "end": v(-15, 108) * mm});
            skLineSegment(sketch, "E80", {"start": v(-15, 108) * mm, "end": v(-15, 120) * mm});
            skArc(sketch, "E81", {"start": v(15, 120) * mm, "mid": v(0, 135) * mm, "end": v(-15, 120) * mm});
            skLineSegment(sketch, "E82", {"start": v(15, 120) * mm, "end": v(15, 108) * mm});
            skLineSegment(sketch, "E83", {"start": v(15, 108) * mm, "end": v(33, 90) * mm});
            skCircle(sketch, "E84", {"center": v(0, 120) * mm, "radius": 6 * mm});
            skLineSegment(sketch, "E85", {"start": v(0, 120) * mm, "end": v(0, 90) * mm, "construction": true});
            skLineSegment(sketch, "E86", {"start": v(-15, 108) * mm, "end": v(-15, 90) * mm, "construction": true});
            skLineSegment(sketch, "E87", {"start": v(15, 108) * mm, "end": v(15, 90) * mm, "construction": true});
            skLineSegment(sketch, "E88", {"start": v(-15, 90) * mm, "end": v(-33, 90) * mm, "construction": true});
            skLineSegment(sketch, "E89", {"start": v(15, 90) * mm, "end": v(33, 90) * mm, "construction": true});
            skLineSegment(sketch, "E90", {"start": v(0, 0) * mm, "end": v(80, 0) * mm, "construction": true});
            skLineSegment(sketch, "E91.MirrorCS", {"start": v(-15, -108) * mm, "end": v(-15, -120) * mm});
            skLineSegment(sketch, "E92.MirrorCS", {"start": v(15, -120) * mm, "end": v(15, -108) * mm});
            skCircle(sketch, "E93.MirrorC", {"center": v(0, -120) * mm, "radius": 6 * mm});
            skArc(sketch, "E94.MirrorCS", {"start": v(15, -120) * mm, "mid": v(0, -135) * mm, "end": v(-15, -120) * mm});
            skLineSegment(sketch, "E95.MirrorCS", {"start": v(15, -108) * mm, "end": v(33, -90) * mm});
            skLineSegment(sketch, "E96.MirrorCS", {"start": v(-33, -90) * mm, "end": v(-15, -108) * mm});
            skSolve(sketch);
        }
        {
            var Q0;
            {var subQ0=sQuery(id+"F16.wireOp",EDGE,"E79");Q0=makeQuery(id+"F16.imprint","IMPRINT",FACE,{"disambiguationData":[TD([[makeQuery(id+"F16.imprint","IMPRINT",EDGE,{"derivedFrom":subQ0}),-1.0]])]});}
            var Q1;
            Q1=makeQuery(id+"F16.imprint","IMPRINT",FACE,{"disambiguationData":[TD([[makeQuery(id+"F16.imprint","IMPRINT",EDGE,{"derivedFrom":makeQuery(id+"F1.opExtrude","CAP_EDGE",EDGE,{"disambiguationData":[OSD([sQuery(id+"F0.wireOp",EDGE,"E1.left")])],"isStart":true})}),-1.0]])]});
            var Q2;
            Q2=makeQuery(id+"F16.imprint","IMPRINT",FACE,{"disambiguationData":[TD([[makeQuery(id+"F16.imprint","IMPRINT",EDGE,{"derivedFrom":sQuery(id+"F16.wireOp",EDGE,"E91.MirrorCS")}),1.0]])]});
            var Q3;
            Q3=makeQuery(id+"F2.opExtrude","CAP_FACE",FACE,{"disambiguationData":[OSD([sQuery(id+"F0.wireOp",EDGE,"E12"),sQuery(id+"F0.wireOp",EDGE,"E13"),sQuery(id+"F0.wireOp",EDGE,"E14"),sQuery(id+"F0.wireOp",EDGE,"E15"),sQuery(id+"F0.wireOp",EDGE,"E17.filletArc"),sQuery(id+"F0.wireOp",EDGE,"E18.filletArc"),sQuery(id+"F0.wireOp",EDGE,"E19.filletArc"),sQuery(id+"F0.wireOp",EDGE,"E20.filletArc"),sQuery(id+"F0.wireOp",EDGE,"E25.0"),sQuery(id+"F0.wireOp",EDGE,"E25.1"),sQuery(id+"F0.wireOp",EDGE,"E25.2"),sQuery(id+"F0.wireOp",EDGE,"E25.3"),sQuery(id+"F0.wireOp",EDGE,"E25.4"),sQuery(id+"F0.wireOp",EDGE,"E25.5"),sQuery(id+"F0.wireOp",EDGE,"E25.6"),sQuery(id+"F0.wireOp",EDGE,"E25.7")])],"isStart":false});
            extrude(context, id + "F17", {"entities" : qUnion([Q0, Q1, Q2]), "operationType" : NewBodyOperationType.ADD, "endBound" : BoundingType.UP_TO_SURFACE, "endBoundEntityFace" : qUnion([Q3]), "depth" : 25 * mm});
        }
    });
